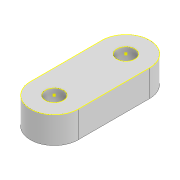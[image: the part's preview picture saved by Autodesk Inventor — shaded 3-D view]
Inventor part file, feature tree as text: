
AUTODESK INVENTOR PART (.ipt)
format: ipt  version: 2022 (Build 260153000, 153)  size: 98,304 bytes
history: native  units: mm
features: sketch x2, extrude x1, projected_geometry x1
ambient origin geometry x8: Origin, YZ Plane, XZ Plane, XY Plane, X Axis, Y Axis, Z Axis, Center Point
bodies: Solid1 (feature_tree)
feature tree (4):
  extrude  "Extrusion1"  Depth=8.0mm
  sketch  "Sketch2"  dims[d3=3.0mm d4=6.0mm d5=4.5mm d6=0.0mm]
  sketch  "Sketch1"  dims[d1=8.0mm d2=3.0mm]
  projected_geometry  "Projected Loop1"
